# Revit family: revitupgrade
name_source: partatom
category: Furniture
units: mm (PartAtom-declared; Revit-internal decimal feet)

## family parameters
Always vertical = Yes
Cut with Voids When Loaded = No
Enable Cutting in Views = No
OmniClass Number = 23.40.70.14.64.11
OmniClass Title = Office Furniture
Render Appearance Source = Family Geometry
Room Calculation Point = No
Shared = No
Work Plane-Based = No

## types (2) — shared parameters
Arm Support = Steelcase - 6205 Black
Assembly Code = E2020200
Base = Steelcase - 6205 Black
Caster = Yes
Default Elevation = 0.00 mm
Description = Gesture is the first chair designed to support our interactions with today's technologies.
Fixed Arm = No
Glide = No
Manufacturer = Steelcase
Release Date = October 2024
Reverse 4D Arm = No
URL = https://www.steelcase.com

## per-type parameters (varying)
| type | Style Number(s) |
| Wrapp Back | 442A40,442A40CN |
| Shell Back | 442A30,442A30CN |

type visibility flags: 2 boolean params named "<type name>" — each type sets only its own to Yes (folded from table)

## geometry (parser evidence)
native form markers: Sweep x3
no freeform markers — native parametric forms only
